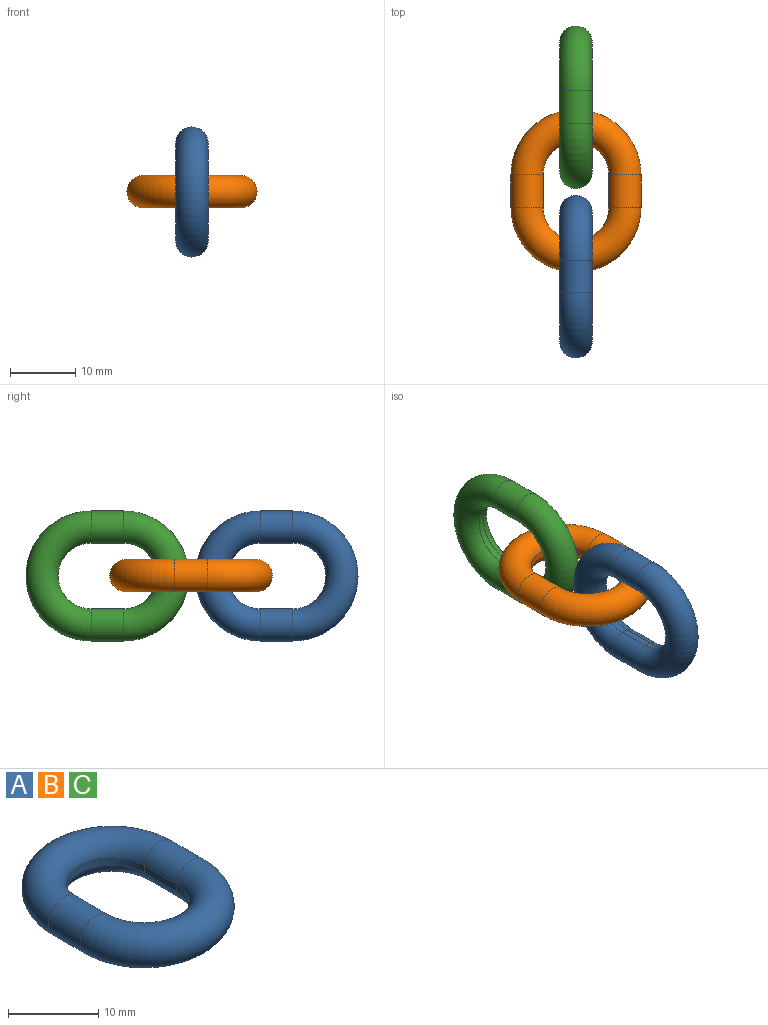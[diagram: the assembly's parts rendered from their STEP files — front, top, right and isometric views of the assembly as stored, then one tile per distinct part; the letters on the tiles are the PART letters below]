
ASSEMBLY  parts=3 mates=1
PART A: 8 faces, bbox 21.6x26.6x5 mm
  f0: plane 5x1mm, normal (1,0,0), area 5mm2, adj f1,f2,f6
  f1: cylinder r=2.5mm len=5mm, axis (0,1,0), area 73.5mm2, adj f0,f3,f7
  f2: cylinder r=5.05mm len=10.1mm, axis (0,0,-1), area 15.9mm2, adj f0,f3,f4
  f3: torus R=7.5mm, axis (0,0,-1), area 354.2mm2, adj f1,f2,f5
  f4: plane 5x1mm, normal (-1,0,0), area 5mm2, adj f2,f5,f6
  f5: cylinder r=2.5mm len=5mm, axis (0,-1,0), area 73.5mm2, adj f3,f4,f7
  f6: cylinder r=5.05mm len=10.1mm, axis (0,0,-1), area 15.9mm2, adj f0,f4,f7
  f7: torus R=7.5mm, axis (0,0,-1), area 354.2mm2, adj f1,f5,f6
PART B: same geometry as A
PART C: same geometry as A
PLACE A rot(axis=(0,1,0),90deg) t=(1.17,-10.44,0.05)mm
PLACE B t=(1.19,2.72,0.1)mm fixed
PLACE C rot(axis=(0,1,0),90deg) t=(1.17,15.6,0.05)mm
MATE parallel C.f2 <-> A.f2  axis (1,0,0) through (1.17,10.6,0.05)mm
